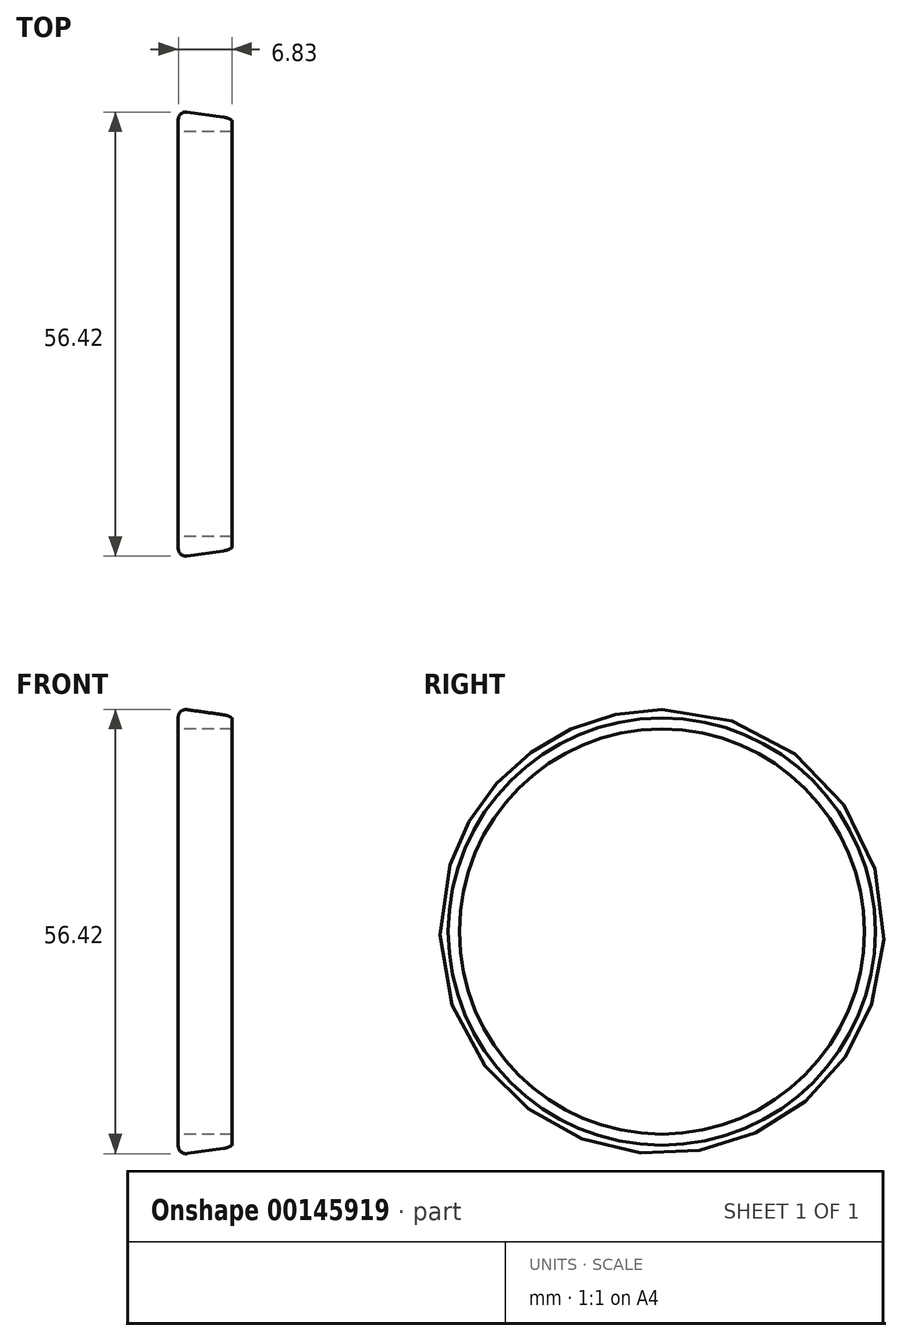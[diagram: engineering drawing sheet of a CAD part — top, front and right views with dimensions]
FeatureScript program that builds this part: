
annotation { "Feature Type Name" : "Feature", "Feature Type Description" : "" }
export const myFeature = defineFeature(function(context is Context, id is Id, definition is map)
    precondition{}
    {
        {
            var Q0;
            Q0=qCreatedBy(makeId("Front.planeOp"),FACE);
            var sketch = newSketch(context, id + "F0", { "sketchPlane" : qUnion([Q0])});
            skLineSegment(sketch, "E0", {"start": v(-17.01, 25.73) * mm, "end": v(-10.18, 25.73) * mm});
            skPoint(sketch, "E1.visualSharp", {"position": v(-17.01, 25.44) * mm});
            skLineSegment(sketch, "E2", {"start": v(-11.26, 27.54) * mm, "end": v(-15.92, 28.2) * mm});
            skLineSegment(sketch, "E3", {"start": v(-17.01, 27.25) * mm, "end": v(-17.01, 25.73) * mm});
            skPoint(sketch, "E4.visualSharp", {"position": v(-17.01, 28.35) * mm});
            skArc(sketch, "E4.filletArc", {"start": v(-15.92, 28.2) * mm, "mid": v(-16.68, 27.97) * mm, "end": v(-17.01, 27.25) * mm});
            skPoint(sketch, "E5.visualSharp", {"position": v(-10.18, 27.4) * mm});
            skArc(sketch, "E5.filletArc", {"start": v(-9.54, 26.52) * mm, "mid": v(-10.3, 27.2) * mm, "end": v(-11.26, 27.54) * mm});
            skLineSegment(sketch, "E6", {"start": v(-10.18, 25.73) * mm, "end": v(-10.18, 27.14) * mm});
            skLineSegment(sketch, "E7", {"start": v(-17.52, 0) * mm, "end": v(-4, 0) * mm});
            skSolve(sketch);
        }
        {
            var Q0;
            Q0=makeQuery(id+"F0.imprint","IMPRINT",FACE,{"disambiguationData":[TD([[makeQuery(id+"F0.imprint","IMPRINT",EDGE,{"derivedFrom":sQuery(id+"F0.wireOp",EDGE,"E0")}),1.0]])]});
            var Q1;
            Q1=sQuery(id+"F0.wireOp",EDGE,"E7");
            revolve(context, id + "F1", {"entities" : qUnion([Q0]), "axis" : qUnion([Q1]), "revolveType" : RevolveType.FULL});
        }
    });
